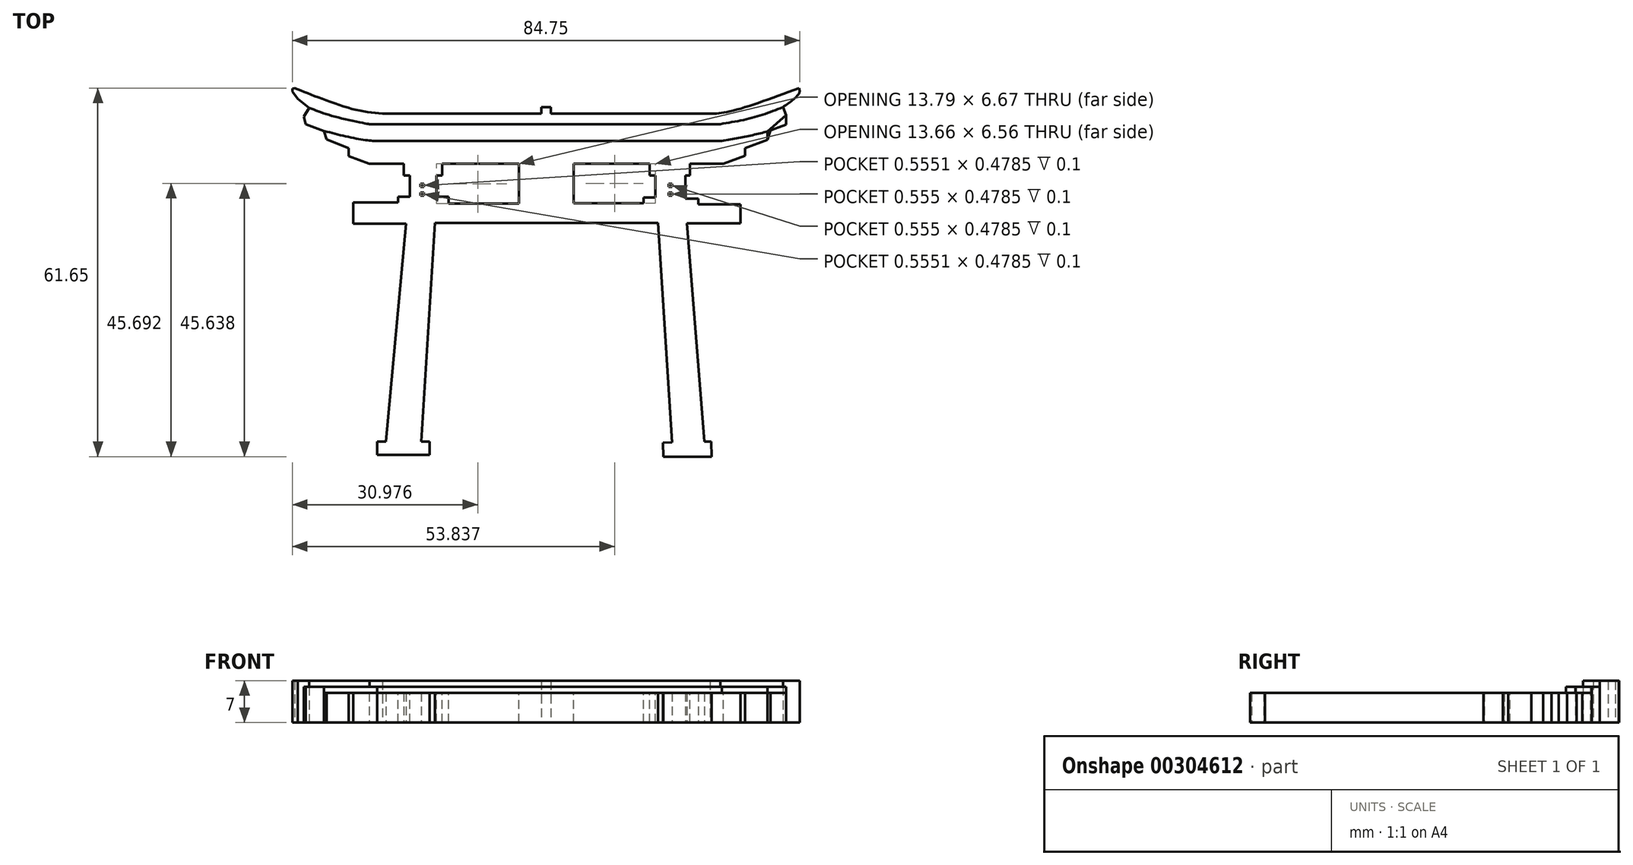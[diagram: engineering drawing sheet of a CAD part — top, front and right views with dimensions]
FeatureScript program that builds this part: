
annotation { "Feature Type Name" : "Feature", "Feature Type Description" : "" }
export const myFeature = defineFeature(function(context is Context, id is Id, definition is map)
    precondition{}
    {
        {
            var Q0;
            Q0=qCreatedBy(makeId("Top.planeOp"),FACE);
            var sketch = newSketch(context, id + "F0", { "sketchPlane" : qUnion([Q0])});
            skLineSegment(sketch, "E0", {"start": v(-21.15, -26.03) * mm, "end": v(-19.72, -26.03) * mm});
            skLineSegment(sketch, "E1", {"start": v(-19.72, -26.03) * mm, "end": v(-19.72, -28.26) * mm});
            skLineSegment(sketch, "E2", {"start": v(-19.72, -28.26) * mm, "end": v(-27.04, -28.26) * mm});
            skLineSegment(sketch, "E3", {"start": v(-23.64, 10.47) * mm, "end": v(-27.04, -26.03) * mm});
            skLineSegment(sketch, "E4", {"start": v(-27.04, -28.26) * mm, "end": v(-28.48, -28.26) * mm});
            skLineSegment(sketch, "E5", {"start": v(-28.48, -28.26) * mm, "end": v(-28.48, -26.03) * mm});
            skLineSegment(sketch, "E6", {"start": v(-28.48, -26.03) * mm, "end": v(-27.04, -26.03) * mm});
            skLineSegment(sketch, "E7", {"start": v(-23.64, 10.47) * mm, "end": v(-32.47, 10.47) * mm});
            skLineSegment(sketch, "E8", {"start": v(-32.47, 10.47) * mm, "end": v(-32.47, 13.97) * mm});
            skLineSegment(sketch, "E9", {"start": v(-23.34, 18.48) * mm, "end": v(-24.03, 18.48) * mm});
            skLineSegment(sketch, "E10", {"start": v(-24.03, 18.48) * mm, "end": v(-24.03, 20.45) * mm});
            skLineSegment(sketch, "E11", {"start": v(-24.03, 20.45) * mm, "end": v(-29.85, 20.45) * mm});
            skLineSegment(sketch, "E12", {"start": v(-29.85, 20.45) * mm, "end": v(-33.28, 21.76) * mm});
            skLineSegment(sketch, "E13", {"start": v(-33.28, 21.76) * mm, "end": v(-33.28, 23.07) * mm});
            skLineSegment(sketch, "E14", {"start": v(-33.28, 23.07) * mm, "end": v(-36.94, 24.53) * mm});
            skLineSegment(sketch, "E15", {"start": v(-36.94, 24.53) * mm, "end": v(-37.36, 25.95) * mm});
            skLineSegment(sketch, "E16", {"start": v(-37.36, 25.95) * mm, "end": v(-40.42, 27.1) * mm});
            skLineSegment(sketch, "E17", {"start": v(-40.42, 27.1) * mm, "end": v(-40.77, 28.34) * mm});
            skLineSegment(sketch, "E18", {"start": v(-40.77, 28.34) * mm, "end": v(-39.86, 29.83) * mm});
            skLineSegment(sketch, "E19", {"start": v(-39.86, 29.83) * mm, "end": v(-41.78, 31.32) * mm});
            skLineSegment(sketch, "E20", {"start": v(-41.78, 31.32) * mm, "end": v(-42.66, 32.53) * mm});
            skLineSegment(sketch, "E21", {"start": v(-42.66, 32.53) * mm, "end": v(-42.66, 33.02) * mm});
            skLineSegment(sketch, "E22", {"start": v(-42.66, 33.02) * mm, "end": v(-42.3, 33.13) * mm});
            skFitSpline(sketch, "E23", {"points": [v(-42.3, 33.13) * mm, v(-38.26, 31.54) * mm, v(-32.27, 29.54) * mm, v(-27.63, 28.83) * mm], "startDerivative": vector(12.27, -4.87) * mm, "endDerivative": vector(13.88, -1.37) * mm});
            skLineSegment(sketch, "E24", {"start": v(-27.63, 28.83) * mm, "end": v(-1.04, 28.83) * mm});
            skLineSegment(sketch, "E25", {"start": v(-1.04, 28.83) * mm, "end": v(-1.04, 29.95) * mm});
            skLineSegment(sketch, "E26", {"start": v(-1.04, 29.95) * mm, "end": v(0.56, 29.95) * mm});
            skLineSegment(sketch, "E27", {"start": v(0.56, 29.95) * mm, "end": v(0.56, 28.83) * mm});
            skLineSegment(sketch, "E28", {"start": v(0.56, 28.83) * mm, "end": v(27.15, 28.83) * mm});
            skFitSpline(sketch, "E29", {"points": [v(27.15, 28.83) * mm, v(30.3, 29.2) * mm, v(42.01, 33.12) * mm], "startDerivative": vector(7.99, 0.25) * mm, "endDerivative": vector(20.39, 7.52) * mm});
            skFitSpline(sketch, "E30", {"points": [v(42.01, 33.12) * mm, v(42.01, 32.3) * mm, v(39.3, 29.94) * mm], "startDerivative": vector(0.65, -2.38) * mm, "endDerivative": vector(-5.38, -3.62) * mm});
            skLineSegment(sketch, "E31", {"start": v(39.3, 29.94) * mm, "end": v(39.86, 28.6) * mm});
            skLineSegment(sketch, "E32", {"start": v(39.86, 28.6) * mm, "end": v(39.86, 27) * mm});
            skLineSegment(sketch, "E33", {"start": v(39.86, 27) * mm, "end": v(36.76, 25.88) * mm});
            skLineSegment(sketch, "E34", {"start": v(36.76, 25.88) * mm, "end": v(36.76, 24.44) * mm});
            skLineSegment(sketch, "E35", {"start": v(36.76, 24.44) * mm, "end": v(33, 23.07) * mm});
            skLineSegment(sketch, "E36", {"start": v(33, 23.07) * mm, "end": v(33, 21.83) * mm});
            skLineSegment(sketch, "E37", {"start": v(33, 21.83) * mm, "end": v(31.69, 20.91) * mm});
            skLineSegment(sketch, "E38", {"start": v(31.69, 20.91) * mm, "end": v(29.33, 20.2) * mm});
            skLineSegment(sketch, "E39", {"start": v(29.33, 20.2) * mm, "end": v(23.78, 20.2) * mm});
            skLineSegment(sketch, "E40", {"start": v(23.78, 20.2) * mm, "end": v(23.78, 18.16) * mm});
            skLineSegment(sketch, "E41", {"start": v(23.78, 18.16) * mm, "end": v(23, 18.16) * mm});
            skLineSegment(sketch, "E42", {"start": v(23, 18.16) * mm, "end": v(23, 14.64) * mm});
            skLineSegment(sketch, "E43", {"start": v(23, 14.64) * mm, "end": v(25.15, 14.64) * mm});
            skLineSegment(sketch, "E44", {"start": v(25.15, 14.64) * mm, "end": v(25.15, 13.7) * mm});
            skLineSegment(sketch, "E45", {"start": v(25.15, 13.7) * mm, "end": v(32.2, 13.7) * mm});
            skLineSegment(sketch, "E46", {"start": v(32.2, 13.7) * mm, "end": v(32.2, 10.51) * mm});
            skLineSegment(sketch, "E47", {"start": v(32.2, 10.51) * mm, "end": v(23.23, 10.51) * mm});
            skLineSegment(sketch, "E48", {"start": v(23.23, 10.51) * mm, "end": v(26.16, -26.03) * mm});
            skPoint(sketch, "E48.endSnap0", {"position": v(-20.43, -26.03) * mm});
            skLineSegment(sketch, "E49", {"start": v(27.39, -28.52) * mm, "end": v(19.31, -28.52) * mm});
            skLineSegment(sketch, "E50", {"start": v(19.31, -28.52) * mm, "end": v(19.25, -26.2) * mm});
            skLineSegment(sketch, "E51", {"start": v(19.25, -26.2) * mm, "end": v(20.8, -26.15) * mm});
            skLineSegment(sketch, "E52", {"start": v(20.8, -26.15) * mm, "end": v(18.45, 10.58) * mm});
            skLineSegment(sketch, "E53", {"start": v(18.45, 10.58) * mm, "end": v(-18.84, 10.58) * mm});
            skLineSegment(sketch, "E54", {"start": v(-18.84, 10.58) * mm, "end": v(-21.15, -26.03) * mm});
            skLineSegment(sketch, "E55", {"start": v(26.16, -26.03) * mm, "end": v(27.3, -26.03) * mm});
            skLineSegment(sketch, "E56", {"start": v(27.3, -26.03) * mm, "end": v(27.39, -28.52) * mm});
            skLineSegment(sketch, "E57", {"start": v(-23.34, 14.75) * mm, "end": v(-25.46, 14.75) * mm});
            skLineSegment(sketch, "E58", {"start": v(-25.46, 14.75) * mm, "end": v(-25.46, 13.97) * mm});
            skLineSegment(sketch, "E59", {"start": v(-25.46, 13.97) * mm, "end": v(-32.47, 13.97) * mm});
            skLineSegment(sketch, "E60", {"start": v(-23.34, 14.75) * mm, "end": v(-23.34, 18.48) * mm});
            skLineSegment(sketch, "E61", {"start": v(36.76, 24.44) * mm, "end": v(37.21, 26.05) * mm});
            skLineSegment(sketch, "E62", {"start": v(37.21, 26.05) * mm, "end": v(39.86, 27) * mm});
            skSolve(sketch);
        }
        {
            var Q0;
            Q0=makeQuery(id+"F0.imprint","IMPRINT",FACE,{"disambiguationData":[TD([[makeQuery(id+"F0.imprint","IMPRINT",EDGE,{"derivedFrom":sQuery(id+"F0.wireOp",EDGE,"E0")}),-1.0]])]});
            extrude(context, id + "F1", {"entities" : qUnion([Q0]), "depth" : 5 * mm});
        }
        {
            var Q0;
            Q0=makeQuery(id+"F1.opExtrude","CAP_FACE",FACE,{"disambiguationData":[OSD([sQuery(id+"F0.wireOp",EDGE,"E0"),sQuery(id+"F0.wireOp",EDGE,"E1"),sQuery(id+"F0.wireOp",EDGE,"E2"),sQuery(id+"F0.wireOp",EDGE,"E3"),sQuery(id+"F0.wireOp",EDGE,"E4"),sQuery(id+"F0.wireOp",EDGE,"E5"),sQuery(id+"F0.wireOp",EDGE,"E6"),sQuery(id+"F0.wireOp",EDGE,"E7"),sQuery(id+"F0.wireOp",EDGE,"E8"),sQuery(id+"F0.wireOp",EDGE,"E9"),sQuery(id+"F0.wireOp",EDGE,"E10"),sQuery(id+"F0.wireOp",EDGE,"E11"),sQuery(id+"F0.wireOp",EDGE,"E12"),sQuery(id+"F0.wireOp",EDGE,"E13"),sQuery(id+"F0.wireOp",EDGE,"E14"),sQuery(id+"F0.wireOp",EDGE,"E15"),sQuery(id+"F0.wireOp",EDGE,"E16"),sQuery(id+"F0.wireOp",EDGE,"E17"),sQuery(id+"F0.wireOp",EDGE,"E18"),sQuery(id+"F0.wireOp",EDGE,"E19"),sQuery(id+"F0.wireOp",EDGE,"E20"),sQuery(id+"F0.wireOp",EDGE,"E21"),sQuery(id+"F0.wireOp",EDGE,"E22"),sQuery(id+"F0.wireOp",EDGE,"E23"),sQuery(id+"F0.wireOp",EDGE,"E24"),sQuery(id+"F0.wireOp",EDGE,"E25"),sQuery(id+"F0.wireOp",EDGE,"E26"),sQuery(id+"F0.wireOp",EDGE,"E27"),sQuery(id+"F0.wireOp",EDGE,"E28"),sQuery(id+"F0.wireOp",EDGE,"E29"),sQuery(id+"F0.wireOp",EDGE,"E30"),sQuery(id+"F0.wireOp",EDGE,"E31"),sQuery(id+"F0.wireOp",EDGE,"E32"),sQuery(id+"F0.wireOp",EDGE,"E33"),sQuery(id+"F0.wireOp",EDGE,"E34"),sQuery(id+"F0.wireOp",EDGE,"E35"),sQuery(id+"F0.wireOp",EDGE,"E36"),sQuery(id+"F0.wireOp",EDGE,"E37"),sQuery(id+"F0.wireOp",EDGE,"E38"),sQuery(id+"F0.wireOp",EDGE,"E39"),sQuery(id+"F0.wireOp",EDGE,"E40"),sQuery(id+"F0.wireOp",EDGE,"E41"),sQuery(id+"F0.wireOp",EDGE,"E42"),sQuery(id+"F0.wireOp",EDGE,"E43"),sQuery(id+"F0.wireOp",EDGE,"E44"),sQuery(id+"F0.wireOp",EDGE,"E45"),sQuery(id+"F0.wireOp",EDGE,"E46"),sQuery(id+"F0.wireOp",EDGE,"E47"),sQuery(id+"F0.wireOp",EDGE,"E48"),sQuery(id+"F0.wireOp",EDGE,"E49"),sQuery(id+"F0.wireOp",EDGE,"E50"),sQuery(id+"F0.wireOp",EDGE,"E51"),sQuery(id+"F0.wireOp",EDGE,"E52"),sQuery(id+"F0.wireOp",EDGE,"E53"),sQuery(id+"F0.wireOp",EDGE,"E54"),sQuery(id+"F0.wireOp",EDGE,"E55"),sQuery(id+"F0.wireOp",EDGE,"E56"),sQuery(id+"F0.wireOp",EDGE,"E57"),sQuery(id+"F0.wireOp",EDGE,"E58"),sQuery(id+"F0.wireOp",EDGE,"E59"),sQuery(id+"F0.wireOp",EDGE,"E60")])],"isStart":false});
            var sketch = newSketch(context, id + "F2", { "sketchPlane" : qUnion([Q0])});
            skLineSegment(sketch, "E63", {"start": v(-17.65, 20.45) * mm, "end": v(-17.65, 18.48) * mm});
            skLineSegment(sketch, "E64", {"start": v(-17.65, 18.48) * mm, "end": v(-18.58, 18.48) * mm});
            skLineSegment(sketch, "E65", {"start": v(-18.58, 18.48) * mm, "end": v(-18.58, 14.95) * mm});
            skLineSegment(sketch, "E66", {"start": v(-18.58, 14.95) * mm, "end": v(-16.58, 14.95) * mm});
            skLineSegment(sketch, "E67", {"start": v(-16.58, 14.95) * mm, "end": v(-16.58, 13.78) * mm});
            skLineSegment(sketch, "E68", {"start": v(-16.58, 13.78) * mm, "end": v(-4.79, 13.78) * mm});
            skLineSegment(sketch, "E69", {"start": v(-4.79, 13.78) * mm, "end": v(-4.79, 20.45) * mm});
            skLineSegment(sketch, "E70", {"start": v(-4.79, 20.45) * mm, "end": v(-17.65, 20.45) * mm});
            skLineSegment(sketch, "E71", {"start": v(17.04, 20.45) * mm, "end": v(17.04, 18.48) * mm});
            skLineSegment(sketch, "E72", {"start": v(17.04, 18.48) * mm, "end": v(18, 18.48) * mm});
            skLineSegment(sketch, "E73", {"start": v(18, 18.48) * mm, "end": v(18, 14.81) * mm});
            skLineSegment(sketch, "E74", {"start": v(18, 14.81) * mm, "end": v(16.02, 14.81) * mm});
            skLineSegment(sketch, "E75", {"start": v(16.02, 14.81) * mm, "end": v(16.02, 13.9) * mm});
            skLineSegment(sketch, "E76", {"start": v(16.02, 13.9) * mm, "end": v(4.35, 13.9) * mm});
            skLineSegment(sketch, "E77", {"start": v(4.35, 13.9) * mm, "end": v(4.35, 20.45) * mm});
            skLineSegment(sketch, "E78", {"start": v(4.35, 20.45) * mm, "end": v(17.04, 20.45) * mm});
            skSolve(sketch);
        }
        {
            var Q0;
            Q0=makeQuery(id+"F2.imprint","IMPRINT",FACE,{"disambiguationData":[TD([[makeQuery(id+"F2.imprint","IMPRINT",EDGE,{"derivedFrom":sQuery(id+"F2.wireOp",EDGE,"E63")}),1.0]])]});
            var Q1;
            Q1=makeQuery(id+"F2.imprint","IMPRINT",FACE,{"disambiguationData":[TD([[makeQuery(id+"F2.imprint","IMPRINT",EDGE,{"derivedFrom":sQuery(id+"F2.wireOp",EDGE,"E71")}),-1.0]])]});
            extrude(context, id + "F3", {"entities" : qUnion([Q0, Q1]), "operationType" : NewBodyOperationType.REMOVE, "endBound" : BoundingType.THROUGH_ALL, "oppositeDirection" : true, "depth" : 25 * mm});
        }
        {
            var Q0;
            {var subQ0=sQuery(id+"F0.wireOp",EDGE,"E45");var subQ1=sQuery(id+"F0.wireOp",EDGE,"E44");var subQ2=sQuery(id+"F0.wireOp",EDGE,"E43");var subQ3=sQuery(id+"F0.wireOp",EDGE,"E42");var subQ4=sQuery(id+"F0.wireOp",EDGE,"E41");var subQ5=sQuery(id+"F0.wireOp",EDGE,"E40");var subQ6=sQuery(id+"F0.wireOp",EDGE,"E39");var subQ7=sQuery(id+"F0.wireOp",EDGE,"E38");var subQ8=sQuery(id+"F0.wireOp",EDGE,"E37");var subQ9=sQuery(id+"F0.wireOp",EDGE,"E36");var subQ10=sQuery(id+"F0.wireOp",EDGE,"E35");var subQ11=sQuery(id+"F0.wireOp",EDGE,"E34");var subQ12=sQuery(id+"F0.wireOp",EDGE,"E33");var subQ13=sQuery(id+"F0.wireOp",EDGE,"E32");var subQ14=sQuery(id+"F0.wireOp",EDGE,"E31");var subQ15=sQuery(id+"F0.wireOp",EDGE,"E30");var subQ16=sQuery(id+"F0.wireOp",EDGE,"E29");var subQ17=sQuery(id+"F0.wireOp",EDGE,"E28");var subQ18=sQuery(id+"F0.wireOp",EDGE,"E27");var subQ19=sQuery(id+"F0.wireOp",EDGE,"E26");var subQ20=sQuery(id+"F0.wireOp",EDGE,"E25");var subQ21=sQuery(id+"F0.wireOp",EDGE,"E24");var subQ22=sQuery(id+"F0.wireOp",EDGE,"E23");var subQ23=sQuery(id+"F0.wireOp",EDGE,"E9");var subQ24=sQuery(id+"F0.wireOp",EDGE,"E8");var subQ25=sQuery(id+"F0.wireOp",EDGE,"E7");var subQ26=sQuery(id+"F0.wireOp",EDGE,"E6");var subQ27=sQuery(id+"F0.wireOp",EDGE,"E5");var subQ28=sQuery(id+"F0.wireOp",EDGE,"E10");var subQ29=sQuery(id+"F0.wireOp",EDGE,"E46");var subQ30=sQuery(id+"F0.wireOp",EDGE,"E0");var subQ31=sQuery(id+"F0.wireOp",EDGE,"E22");var subQ32=sQuery(id+"F0.wireOp",EDGE,"E3");var subQ33=sQuery(id+"F0.wireOp",EDGE,"E1");var subQ34=sQuery(id+"F0.wireOp",EDGE,"E4");var subQ35=sQuery(id+"F0.wireOp",EDGE,"E2");var subQ36=sQuery(id+"F0.wireOp",EDGE,"E11");var subQ37=sQuery(id+"F0.wireOp",EDGE,"E12");var subQ38=sQuery(id+"F0.wireOp",EDGE,"E13");var subQ39=sQuery(id+"F0.wireOp",EDGE,"E14");var subQ40=sQuery(id+"F0.wireOp",EDGE,"E15");var subQ41=sQuery(id+"F0.wireOp",EDGE,"E16");var subQ42=sQuery(id+"F0.wireOp",EDGE,"E17");var subQ43=sQuery(id+"F0.wireOp",EDGE,"E18");var subQ44=sQuery(id+"F0.wireOp",EDGE,"E19");var subQ45=sQuery(id+"F0.wireOp",EDGE,"E20");var subQ46=sQuery(id+"F0.wireOp",EDGE,"E21");var subQ47=sQuery(id+"F0.wireOp",EDGE,"E47");var subQ48=sQuery(id+"F0.wireOp",EDGE,"E48");var subQ49=sQuery(id+"F0.wireOp",EDGE,"E49");var subQ50=sQuery(id+"F0.wireOp",EDGE,"E50");var subQ51=sQuery(id+"F0.wireOp",EDGE,"E51");var subQ52=sQuery(id+"F0.wireOp",EDGE,"E52");var subQ53=sQuery(id+"F0.wireOp",EDGE,"E53");var subQ54=sQuery(id+"F0.wireOp",EDGE,"E54");var subQ55=sQuery(id+"F0.wireOp",EDGE,"E55");var subQ56=sQuery(id+"F0.wireOp",EDGE,"E56");var subQ57=sQuery(id+"F0.wireOp",EDGE,"E57");var subQ58=sQuery(id+"F0.wireOp",EDGE,"E58");var subQ59=sQuery(id+"F0.wireOp",EDGE,"E59");var subQ60=sQuery(id+"F0.wireOp",EDGE,"E60");Q0=makeQuery(id+"FRBVWJomYvBm3HE_1.boolean.opBoolean","SPLIT",FACE,{"disambiguationData":[TD([makeQuery(id+"F1.opExtrude","SWEPT_FACE",FACE,{"disambiguationData":[OSD([subQ30])]})])],"derivedFrom":makeQuery(id+"F1.opExtrude","CAP_FACE",FACE,{"disambiguationData":[OSD([subQ30,subQ33,subQ35,subQ32,subQ34,subQ27,subQ26,subQ25,subQ24,subQ23,subQ28,subQ36,subQ37,subQ38,subQ39,subQ40,subQ41,subQ42,subQ43,subQ44,subQ45,subQ46,subQ31,subQ22,subQ21,subQ20,subQ19,subQ18,subQ17,subQ16,subQ15,subQ14,subQ13,subQ12,subQ11,subQ10,subQ9,subQ8,subQ7,subQ6,subQ5,subQ4,subQ3,subQ2,subQ1,subQ0,subQ29,subQ47,subQ48,subQ49,subQ50,subQ51,subQ52,subQ53,subQ54,subQ55,subQ56,subQ57,subQ58,subQ59,subQ60])],"isStart":false})});}
            var sketch = newSketch(context, id + "F4", { "sketchPlane" : qUnion([Q0])});
            skFitSpline(sketch, "E79", {"points": [v(-37.36, 25.95) * mm, v(-33.12, 24.92) * mm, v(-29.93, 24.37) * mm, v(-28.48, 24.27) * mm], "startDerivative": vector(10.45, -2.7) * mm, "endDerivative": vector(5.56, -0.21) * mm});
            skLineSegment(sketch, "E80", {"start": v(-28.48, 24.27) * mm, "end": v(29.09, 24.3) * mm});
            skFitSpline(sketch, "E81", {"points": [v(29.09, 24.3) * mm, v(33.26, 25.05) * mm, v(36.76, 25.88) * mm], "startDerivative": vector(8.2, 1.38) * mm, "endDerivative": vector(7.12, 1.81) * mm});
            skFitSpline(sketch, "E82", {"points": [v(-39.86, 29.83) * mm, v(-35.24, 28.27) * mm, v(-29.84, 27.1) * mm, v(-29.77, 27.1) * mm], "startDerivative": vector(8.57, -3.4) * mm, "endDerivative": vector(0.66, 0.12) * mm});
            skLineSegment(sketch, "E83", {"start": v(-29.77, 27.1) * mm, "end": v(28.82, 27.1) * mm});
            skFitSpline(sketch, "E84", {"points": [v(28.82, 27.1) * mm, v(34.5, 28.24) * mm, v(39.3, 29.94) * mm], "startDerivative": vector(11.26, 1.86) * mm, "endDerivative": vector(9.69, 3.82) * mm});
            skLineSegment(sketch, "E85", {"start": v(39.3, 29.94) * mm, "end": v(39.86, 28.6) * mm});
            skLineSegment(sketch, "E86", {"start": v(39.86, 28.6) * mm, "end": v(39.86, 28.6) * mm});
            skLineSegment(sketch, "E87", {"start": v(39.86, 28.6) * mm, "end": v(36.76, 25.88) * mm});
            skLineSegment(sketch, "E88", {"start": v(-39.86, 29.83) * mm, "end": v(-40.77, 28.34) * mm});
            skLineSegment(sketch, "E89", {"start": v(-40.77, 28.34) * mm, "end": v(-40.42, 27.1) * mm});
            skLineSegment(sketch, "E90", {"start": v(-40.42, 27.1) * mm, "end": v(-37.36, 25.95) * mm});
            skSolve(sketch);
        }
        {
            var Q0;
            Q0=makeQuery(id+"F4.imprint","IMPRINT",FACE,{"disambiguationData":[TD([[makeQuery(id+"F4.imprint","IMPRINT",EDGE,{"derivedFrom":sQuery(id+"F4.wireOp",EDGE,"E79")}),1.0]])]});
            extrude(context, id + "F5", {"entities" : qUnion([Q0]), "operationType" : NewBodyOperationType.ADD, "depth" : 1 * mm});
        }
        {
            var Q0;
            {var subQ0=sQuery(id+"F0.wireOp",EDGE,"E27");var subQ2=sQuery(id+"F0.wireOp",EDGE,"E26");var subQ4=sQuery(id+"F0.wireOp",EDGE,"E25");var subQ6=sQuery(id+"F0.wireOp",EDGE,"E24");var subQ8=sQuery(id+"F0.wireOp",EDGE,"E23");var subQ10=sQuery(id+"F0.wireOp",EDGE,"E22");var subQ12=sQuery(id+"F0.wireOp",EDGE,"E18");var subQ13=makeQuery(id+"F1.opExtrude","SWEPT_FACE",FACE,{"disambiguationData":[OSD([subQ12])]});var subQ14=sQuery(id+"F0.wireOp",EDGE,"E19");var subQ16=sQuery(id+"F0.wireOp",EDGE,"E20");var subQ18=sQuery(id+"F0.wireOp",EDGE,"E21");var subQ20=sQuery(id+"F0.wireOp",EDGE,"E28");var subQ22=sQuery(id+"F0.wireOp",EDGE,"E29");var subQ24=sQuery(id+"F0.wireOp",EDGE,"E30");var subQ26=sQuery(id+"F0.wireOp",EDGE,"E31");var subQ28=sQuery(id+"F0.wireOp",EDGE,"E45");var subQ29=sQuery(id+"F0.wireOp",EDGE,"E44");var subQ30=sQuery(id+"F0.wireOp",EDGE,"E43");var subQ31=sQuery(id+"F0.wireOp",EDGE,"E42");var subQ32=sQuery(id+"F0.wireOp",EDGE,"E41");var subQ33=sQuery(id+"F0.wireOp",EDGE,"E40");var subQ34=sQuery(id+"F0.wireOp",EDGE,"E39");var subQ35=sQuery(id+"F0.wireOp",EDGE,"E38");var subQ36=sQuery(id+"F0.wireOp",EDGE,"E37");var subQ37=sQuery(id+"F0.wireOp",EDGE,"E36");var subQ38=sQuery(id+"F0.wireOp",EDGE,"E35");var subQ39=sQuery(id+"F0.wireOp",EDGE,"E34");var subQ40=sQuery(id+"F0.wireOp",EDGE,"E33");var subQ41=sQuery(id+"F0.wireOp",EDGE,"E32");var subQ42=sQuery(id+"F0.wireOp",EDGE,"E9");var subQ43=sQuery(id+"F0.wireOp",EDGE,"E8");var subQ44=sQuery(id+"F0.wireOp",EDGE,"E7");var subQ45=sQuery(id+"F0.wireOp",EDGE,"E6");var subQ46=sQuery(id+"F0.wireOp",EDGE,"E5");var subQ47=sQuery(id+"F0.wireOp",EDGE,"E10");var subQ48=sQuery(id+"F0.wireOp",EDGE,"E46");var subQ49=sQuery(id+"F0.wireOp",EDGE,"E0");var subQ50=sQuery(id+"F0.wireOp",EDGE,"E3");var subQ51=sQuery(id+"F0.wireOp",EDGE,"E1");var subQ52=sQuery(id+"F0.wireOp",EDGE,"E4");var subQ53=sQuery(id+"F0.wireOp",EDGE,"E2");var subQ54=sQuery(id+"F0.wireOp",EDGE,"E11");var subQ55=sQuery(id+"F0.wireOp",EDGE,"E12");var subQ56=sQuery(id+"F0.wireOp",EDGE,"E13");var subQ57=sQuery(id+"F0.wireOp",EDGE,"E14");var subQ58=sQuery(id+"F0.wireOp",EDGE,"E15");var subQ59=sQuery(id+"F0.wireOp",EDGE,"E16");var subQ60=sQuery(id+"F0.wireOp",EDGE,"E17");var subQ61=sQuery(id+"F0.wireOp",EDGE,"E47");var subQ62=sQuery(id+"F0.wireOp",EDGE,"E48");var subQ63=sQuery(id+"F0.wireOp",EDGE,"E49");var subQ64=sQuery(id+"F0.wireOp",EDGE,"E50");var subQ65=sQuery(id+"F0.wireOp",EDGE,"E51");var subQ66=sQuery(id+"F0.wireOp",EDGE,"E52");var subQ67=sQuery(id+"F0.wireOp",EDGE,"E53");var subQ68=sQuery(id+"F0.wireOp",EDGE,"E54");var subQ69=sQuery(id+"F0.wireOp",EDGE,"E55");var subQ70=sQuery(id+"F0.wireOp",EDGE,"E56");var subQ71=sQuery(id+"F0.wireOp",EDGE,"E57");var subQ72=sQuery(id+"F0.wireOp",EDGE,"E58");var subQ73=sQuery(id+"F0.wireOp",EDGE,"E59");var subQ74=sQuery(id+"F0.wireOp",EDGE,"E60");Q0=makeQuery(id+"F5.boolean.opBoolean","SPLIT",FACE,{"disambiguationData":[TD([subQ13])],"derivedFrom":makeQuery(id+"FRBVWJomYvBm3HE_1.boolean.opBoolean","SPLIT",FACE,{"disambiguationData":[TD([makeQuery(id+"F1.opExtrude","SWEPT_FACE",FACE,{"disambiguationData":[OSD([subQ49])]})])],"derivedFrom":makeQuery(id+"F1.opExtrude","CAP_FACE",FACE,{"disambiguationData":[OSD([subQ49,subQ51,subQ53,subQ50,subQ52,subQ46,subQ45,subQ44,subQ43,subQ42,subQ47,subQ54,subQ55,subQ56,subQ57,subQ58,subQ59,subQ60,subQ12,subQ14,subQ16,subQ18,subQ10,subQ8,subQ6,subQ4,subQ2,subQ0,subQ20,subQ22,subQ24,subQ26,subQ41,subQ40,subQ39,subQ38,subQ37,subQ36,subQ35,subQ34,subQ33,subQ32,subQ31,subQ30,subQ29,subQ28,subQ48,subQ61,subQ62,subQ63,subQ64,subQ65,subQ66,subQ67,subQ68,subQ69,subQ70,subQ71,subQ72,subQ73,subQ74])],"isStart":false})})});}
            extrude(context, id + "F6", {"entities" : qUnion([Q0]), "operationType" : NewBodyOperationType.ADD, "depth" : 2 * mm});
        }
        {
            var Q0;
            {var subQ0=sQuery(id+"F0.wireOp",EDGE,"E48");var subQ2=sQuery(id+"F0.wireOp",EDGE,"E47");var subQ5=sQuery(id+"F0.wireOp",EDGE,"E45");var subQ7=sQuery(id+"F0.wireOp",EDGE,"E44");var subQ9=sQuery(id+"F0.wireOp",EDGE,"E43");var subQ11=sQuery(id+"F0.wireOp",EDGE,"E42");var subQ13=sQuery(id+"F0.wireOp",EDGE,"E41");var subQ15=sQuery(id+"F0.wireOp",EDGE,"E40");var subQ17=sQuery(id+"F0.wireOp",EDGE,"E39");var subQ19=sQuery(id+"F0.wireOp",EDGE,"E56");var subQ21=sQuery(id+"F0.wireOp",EDGE,"E9");var subQ23=sQuery(id+"F0.wireOp",EDGE,"E55");var subQ25=sQuery(id+"F0.wireOp",EDGE,"E8");var subQ27=sQuery(id+"F0.wireOp",EDGE,"E54");var subQ29=sQuery(id+"F0.wireOp",EDGE,"E7");var subQ32=sQuery(id+"F0.wireOp",EDGE,"E53");var subQ34=sQuery(id+"F0.wireOp",EDGE,"E6");var subQ37=sQuery(id+"F0.wireOp",EDGE,"E52");var subQ39=sQuery(id+"F0.wireOp",EDGE,"E5");var subQ41=sQuery(id+"F0.wireOp",EDGE,"E57");var subQ43=sQuery(id+"F0.wireOp",EDGE,"E10");var subQ45=sQuery(id+"F0.wireOp",EDGE,"E33");var subQ48=sQuery(id+"F0.wireOp",EDGE,"E46");var subQ50=sQuery(id+"F0.wireOp",EDGE,"E0");var subQ51=makeQuery(id+"F1.opExtrude","SWEPT_FACE",FACE,{"disambiguationData":[OSD([subQ50])]});var subQ52=sQuery(id+"F0.wireOp",EDGE,"E51");var subQ55=sQuery(id+"F0.wireOp",EDGE,"E3");var subQ57=sQuery(id+"F0.wireOp",EDGE,"E49");var subQ60=sQuery(id+"F0.wireOp",EDGE,"E1");var subQ62=sQuery(id+"F0.wireOp",EDGE,"E50");var subQ65=sQuery(id+"F0.wireOp",EDGE,"E4");var subQ66=sQuery(id+"F0.wireOp",EDGE,"E2");var subQ68=sQuery(id+"F0.wireOp",EDGE,"E58");var subQ70=sQuery(id+"F0.wireOp",EDGE,"E11");var subQ72=sQuery(id+"F0.wireOp",EDGE,"E34");var subQ75=sQuery(id+"F0.wireOp",EDGE,"E59");var subQ77=sQuery(id+"F0.wireOp",EDGE,"E12");var subQ79=sQuery(id+"F0.wireOp",EDGE,"E35");var subQ82=sQuery(id+"F0.wireOp",EDGE,"E60");var subQ84=sQuery(id+"F0.wireOp",EDGE,"E13");var subQ86=sQuery(id+"F0.wireOp",EDGE,"E36");var subQ89=sQuery(id+"F0.wireOp",EDGE,"E14");var subQ91=sQuery(id+"F0.wireOp",EDGE,"E37");var subQ94=sQuery(id+"F0.wireOp",EDGE,"E15");var subQ96=sQuery(id+"F0.wireOp",EDGE,"E38");var subQ99=sQuery(id+"F0.wireOp",EDGE,"E16");var subQ109=sQuery(id+"F0.wireOp",EDGE,"E32");var subQ110=sQuery(id+"F0.wireOp",EDGE,"E31");var subQ111=sQuery(id+"F0.wireOp",EDGE,"E30");var subQ112=sQuery(id+"F0.wireOp",EDGE,"E29");var subQ113=sQuery(id+"F0.wireOp",EDGE,"E28");var subQ114=sQuery(id+"F0.wireOp",EDGE,"E27");var subQ115=sQuery(id+"F0.wireOp",EDGE,"E26");var subQ116=sQuery(id+"F0.wireOp",EDGE,"E25");var subQ117=sQuery(id+"F0.wireOp",EDGE,"E24");var subQ118=sQuery(id+"F0.wireOp",EDGE,"E23");var subQ119=sQuery(id+"F0.wireOp",EDGE,"E22");var subQ120=sQuery(id+"F0.wireOp",EDGE,"E17");var subQ121=sQuery(id+"F0.wireOp",EDGE,"E18");var subQ122=sQuery(id+"F0.wireOp",EDGE,"E19");var subQ123=sQuery(id+"F0.wireOp",EDGE,"E20");var subQ124=sQuery(id+"F0.wireOp",EDGE,"E21");Q0=makeQuery(id+"F5.boolean.opBoolean","SPLIT",FACE,{"disambiguationData":[TD([subQ51])],"derivedFrom":makeQuery(id+"FRBVWJomYvBm3HE_1.boolean.opBoolean","SPLIT",FACE,{"disambiguationData":[TD([subQ51])],"derivedFrom":makeQuery(id+"F1.opExtrude","CAP_FACE",FACE,{"disambiguationData":[OSD([subQ50,subQ60,subQ66,subQ55,subQ65,subQ39,subQ34,subQ29,subQ25,subQ21,subQ43,subQ70,subQ77,subQ84,subQ89,subQ94,subQ99,subQ120,subQ121,subQ122,subQ123,subQ124,subQ119,subQ118,subQ117,subQ116,subQ115,subQ114,subQ113,subQ112,subQ111,subQ110,subQ109,subQ45,subQ72,subQ79,subQ86,subQ91,subQ96,subQ17,subQ15,subQ13,subQ11,subQ9,subQ7,subQ5,subQ48,subQ2,subQ0,subQ57,subQ62,subQ52,subQ37,subQ32,subQ27,subQ23,subQ19,subQ41,subQ68,subQ75,subQ82])],"isStart":false})})});}
            var sketch = newSketch(context, id + "F7", { "sketchPlane" : qUnion([Q0])});
            skLineSegment(sketch, "E91", {"start": v(23, 18.48) * mm, "end": v(23, 14.64) * mm});
            skLineSegment(sketch, "E92", {"start": v(23, 18.48) * mm, "end": v(23.78, 18.48) * mm});
            skLineSegment(sketch, "E93", {"start": v(23.78, 18.48) * mm, "end": v(23.78, 20.45) * mm});
            skLineSegment(sketch, "E94", {"start": v(23.78, 20.45) * mm, "end": v(29.33, 20.45) * mm});
            skLineSegment(sketch, "E95", {"start": v(29.33, 20.45) * mm, "end": v(33, 21.83) * mm});
            skSolve(sketch);
        }
        {
            var Q0;
            {var subQ0=sQuery(id+"F7.wireOp",EDGE,"E94");Q0=makeQuery(id+"F7.imprint","IMPRINT",FACE,{"disambiguationData":[TD([[makeQuery(id+"F7.imprint","IMPRINT",EDGE,{"derivedFrom":subQ0}),-1.0]])]});}
            extrude(context, id + "F8", {"entities" : qUnion([Q0]), "operationType" : NewBodyOperationType.REMOVE, "oppositeDirection" : true, "depth" : 25 * mm});
        }
        {
            var Q0;
            Q0=makeQuery(id+"F0.imprint","IMPRINT",FACE,{"disambiguationData":[TD([[makeQuery(id+"F0.imprint","IMPRINT",EDGE,{"derivedFrom":sQuery(id+"F0.wireOp",EDGE,"E33")}),1.0]])]});
            extrude(context, id + "F9", {"entities" : qUnion([Q0]), "depth" : 5 * mm});
        }
        {
            var Q0;
            {var subQ0=sQuery(id+"F0.wireOp",EDGE,"E47");var subQ3=sQuery(id+"F0.wireOp",EDGE,"E45");var subQ5=sQuery(id+"F0.wireOp",EDGE,"E44");var subQ7=sQuery(id+"F0.wireOp",EDGE,"E43");var subQ9=sQuery(id+"F0.wireOp",EDGE,"E42");var subQ11=sQuery(id+"F0.wireOp",EDGE,"E41");var subQ13=sQuery(id+"F0.wireOp",EDGE,"E40");var subQ15=sQuery(id+"F0.wireOp",EDGE,"E39");var subQ17=sQuery(id+"F0.wireOp",EDGE,"E38");var subQ20=sQuery(id+"F0.wireOp",EDGE,"E56");var subQ22=sQuery(id+"F0.wireOp",EDGE,"E9");var subQ24=sQuery(id+"F0.wireOp",EDGE,"E55");var subQ26=sQuery(id+"F0.wireOp",EDGE,"E8");var subQ28=sQuery(id+"F0.wireOp",EDGE,"E54");var subQ30=sQuery(id+"F0.wireOp",EDGE,"E7");var subQ32=sQuery(id+"F0.wireOp",EDGE,"E53");var subQ34=sQuery(id+"F0.wireOp",EDGE,"E6");var subQ37=sQuery(id+"F0.wireOp",EDGE,"E52");var subQ39=sQuery(id+"F0.wireOp",EDGE,"E5");var subQ41=sQuery(id+"F0.wireOp",EDGE,"E51");var subQ44=sQuery(id+"F0.wireOp",EDGE,"E3");var subQ46=sQuery(id+"F0.wireOp",EDGE,"E46");var subQ48=sQuery(id+"F0.wireOp",EDGE,"E0");var subQ49=makeQuery(id+"F1.opExtrude","SWEPT_FACE",FACE,{"disambiguationData":[OSD([subQ48])]});var subQ50=sQuery(id+"F0.wireOp",EDGE,"E48");var subQ52=sQuery(id+"F0.wireOp",EDGE,"E62");var subQ53=sQuery(id+"F0.wireOp",EDGE,"E60");var subQ54=sQuery(id+"F0.wireOp",EDGE,"E59");var subQ55=sQuery(id+"F0.wireOp",EDGE,"E58");var subQ56=sQuery(id+"F0.wireOp",EDGE,"E57");var subQ57=sQuery(id+"F0.wireOp",EDGE,"E50");var subQ58=sQuery(id+"F0.wireOp",EDGE,"E49");var subQ59=sQuery(id+"F0.wireOp",EDGE,"E37");var subQ60=sQuery(id+"F0.wireOp",EDGE,"E36");var subQ61=sQuery(id+"F0.wireOp",EDGE,"E35");var subQ62=sQuery(id+"F0.wireOp",EDGE,"E34");var subQ63=sQuery(id+"F0.wireOp",EDGE,"E33");var subQ64=sQuery(id+"F0.wireOp",EDGE,"E32");var subQ65=sQuery(id+"F0.wireOp",EDGE,"E31");var subQ66=sQuery(id+"F0.wireOp",EDGE,"E30");var subQ67=sQuery(id+"F0.wireOp",EDGE,"E29");var subQ68=sQuery(id+"F0.wireOp",EDGE,"E28");var subQ69=sQuery(id+"F0.wireOp",EDGE,"E27");var subQ70=sQuery(id+"F0.wireOp",EDGE,"E26");var subQ71=sQuery(id+"F0.wireOp",EDGE,"E25");var subQ72=sQuery(id+"F0.wireOp",EDGE,"E24");var subQ73=sQuery(id+"F0.wireOp",EDGE,"E23");var subQ74=sQuery(id+"F0.wireOp",EDGE,"E22");var subQ75=sQuery(id+"F0.wireOp",EDGE,"E21");var subQ76=sQuery(id+"F0.wireOp",EDGE,"E20");var subQ77=sQuery(id+"F0.wireOp",EDGE,"E19");var subQ78=sQuery(id+"F0.wireOp",EDGE,"E18");var subQ79=sQuery(id+"F0.wireOp",EDGE,"E17");var subQ80=sQuery(id+"F0.wireOp",EDGE,"E16");var subQ81=sQuery(id+"F0.wireOp",EDGE,"E15");var subQ82=sQuery(id+"F0.wireOp",EDGE,"E14");var subQ83=sQuery(id+"F0.wireOp",EDGE,"E13");var subQ84=sQuery(id+"F0.wireOp",EDGE,"E12");var subQ85=sQuery(id+"F0.wireOp",EDGE,"E11");var subQ86=sQuery(id+"F0.wireOp",EDGE,"E10");var subQ87=sQuery(id+"F0.wireOp",EDGE,"E4");var subQ88=sQuery(id+"F0.wireOp",EDGE,"E2");var subQ89=sQuery(id+"F0.wireOp",EDGE,"E1");var subQ90=makeQuery(id+"F1.opExtrude","CAP_FACE",FACE,{"disambiguationData":[OSD([subQ48,subQ89,subQ88,subQ44,subQ87,subQ39,subQ34,subQ30,subQ26,subQ22,subQ86,subQ85,subQ84,subQ83,subQ82,subQ81,subQ80,subQ79,subQ78,subQ77,subQ76,subQ75,subQ74,subQ73,subQ72,subQ71,subQ70,subQ69,subQ68,subQ67,subQ66,subQ65,subQ64,subQ63,subQ62,subQ61,subQ60,subQ59,subQ17,subQ15,subQ13,subQ11,subQ9,subQ7,subQ5,subQ3,subQ46,subQ0,subQ50,subQ58,subQ57,subQ41,subQ37,subQ32,subQ28,subQ24,subQ20,subQ56,subQ55,subQ54,subQ53,subQ52])],"isStart":false});Q0=makeQuery(id+"F5.boolean.opBoolean","SPLIT",FACE,{"disambiguationData":[TD([subQ49])],"derivedFrom":makeQuery(id+"FRBVWJomYvBm3HE_1.boolean.opBoolean","SPLIT",FACE,{"disambiguationData":[TD([subQ49])],"derivedFrom":subQ90})});}
            var sketch = newSketch(context, id + "F10", { "sketchPlane" : qUnion([Q0])});
            skLineSegment(sketch, "E96", {"start": v(23, 14.64) * mm, "end": v(23, 18.48) * mm});
            skLineSegment(sketch, "E97", {"start": v(23, 18.48) * mm, "end": v(23.78, 18.48) * mm});
            skSolve(sketch);
        }
        {
            var Q0;
            {var subQ2=sQuery(id+"F10.wireOp",EDGE,"E97");Q0=makeQuery(id+"F10.imprint","IMPRINT",FACE,{"disambiguationData":[TD([[makeQuery(id+"F10.imprint","IMPRINT",EDGE,{"derivedFrom":subQ2}),-1.0]])]});}
            extrude(context, id + "F11", {"entities" : qUnion([Q0]), "operationType" : NewBodyOperationType.REMOVE, "oppositeDirection" : true, "depth" : 25 * mm});
        }
        {
            var Q0;
            {var subQ0=sQuery(id+"F0.wireOp",EDGE,"E47");var subQ3=sQuery(id+"F0.wireOp",EDGE,"E45");var subQ5=sQuery(id+"F0.wireOp",EDGE,"E44");var subQ7=sQuery(id+"F0.wireOp",EDGE,"E43");var subQ9=sQuery(id+"F0.wireOp",EDGE,"E42");var subQ11=sQuery(id+"F0.wireOp",EDGE,"E41");var subQ13=sQuery(id+"F0.wireOp",EDGE,"E40");var subQ15=sQuery(id+"F0.wireOp",EDGE,"E39");var subQ17=sQuery(id+"F0.wireOp",EDGE,"E38");var subQ20=sQuery(id+"F0.wireOp",EDGE,"E56");var subQ22=sQuery(id+"F0.wireOp",EDGE,"E9");var subQ24=sQuery(id+"F0.wireOp",EDGE,"E55");var subQ26=sQuery(id+"F0.wireOp",EDGE,"E8");var subQ28=sQuery(id+"F0.wireOp",EDGE,"E54");var subQ30=sQuery(id+"F0.wireOp",EDGE,"E7");var subQ32=sQuery(id+"F0.wireOp",EDGE,"E53");var subQ34=sQuery(id+"F0.wireOp",EDGE,"E6");var subQ37=sQuery(id+"F0.wireOp",EDGE,"E52");var subQ39=sQuery(id+"F0.wireOp",EDGE,"E5");var subQ41=sQuery(id+"F0.wireOp",EDGE,"E51");var subQ44=sQuery(id+"F0.wireOp",EDGE,"E3");var subQ46=sQuery(id+"F0.wireOp",EDGE,"E46");var subQ48=sQuery(id+"F0.wireOp",EDGE,"E0");var subQ49=makeQuery(id+"F1.opExtrude","SWEPT_FACE",FACE,{"disambiguationData":[OSD([subQ48])]});var subQ50=sQuery(id+"F0.wireOp",EDGE,"E48");var subQ52=sQuery(id+"F0.wireOp",EDGE,"E62");var subQ53=sQuery(id+"F0.wireOp",EDGE,"E60");var subQ54=sQuery(id+"F0.wireOp",EDGE,"E59");var subQ55=sQuery(id+"F0.wireOp",EDGE,"E58");var subQ56=sQuery(id+"F0.wireOp",EDGE,"E57");var subQ57=sQuery(id+"F0.wireOp",EDGE,"E50");var subQ58=sQuery(id+"F0.wireOp",EDGE,"E49");var subQ59=sQuery(id+"F0.wireOp",EDGE,"E37");var subQ60=sQuery(id+"F0.wireOp",EDGE,"E36");var subQ61=sQuery(id+"F0.wireOp",EDGE,"E35");var subQ62=sQuery(id+"F0.wireOp",EDGE,"E34");var subQ63=sQuery(id+"F0.wireOp",EDGE,"E33");var subQ64=sQuery(id+"F0.wireOp",EDGE,"E32");var subQ65=sQuery(id+"F0.wireOp",EDGE,"E31");var subQ66=sQuery(id+"F0.wireOp",EDGE,"E30");var subQ67=sQuery(id+"F0.wireOp",EDGE,"E29");var subQ68=sQuery(id+"F0.wireOp",EDGE,"E28");var subQ69=sQuery(id+"F0.wireOp",EDGE,"E27");var subQ70=sQuery(id+"F0.wireOp",EDGE,"E26");var subQ71=sQuery(id+"F0.wireOp",EDGE,"E25");var subQ72=sQuery(id+"F0.wireOp",EDGE,"E24");var subQ73=sQuery(id+"F0.wireOp",EDGE,"E23");var subQ74=sQuery(id+"F0.wireOp",EDGE,"E22");var subQ75=sQuery(id+"F0.wireOp",EDGE,"E21");var subQ76=sQuery(id+"F0.wireOp",EDGE,"E20");var subQ77=sQuery(id+"F0.wireOp",EDGE,"E19");var subQ78=sQuery(id+"F0.wireOp",EDGE,"E18");var subQ79=sQuery(id+"F0.wireOp",EDGE,"E17");var subQ80=sQuery(id+"F0.wireOp",EDGE,"E16");var subQ81=sQuery(id+"F0.wireOp",EDGE,"E15");var subQ82=sQuery(id+"F0.wireOp",EDGE,"E14");var subQ83=sQuery(id+"F0.wireOp",EDGE,"E13");var subQ84=sQuery(id+"F0.wireOp",EDGE,"E12");var subQ85=sQuery(id+"F0.wireOp",EDGE,"E11");var subQ86=sQuery(id+"F0.wireOp",EDGE,"E10");var subQ87=sQuery(id+"F0.wireOp",EDGE,"E4");var subQ88=sQuery(id+"F0.wireOp",EDGE,"E2");var subQ89=sQuery(id+"F0.wireOp",EDGE,"E1");var subQ90=makeQuery(id+"F1.opExtrude","CAP_FACE",FACE,{"disambiguationData":[OSD([subQ48,subQ89,subQ88,subQ44,subQ87,subQ39,subQ34,subQ30,subQ26,subQ22,subQ86,subQ85,subQ84,subQ83,subQ82,subQ81,subQ80,subQ79,subQ78,subQ77,subQ76,subQ75,subQ74,subQ73,subQ72,subQ71,subQ70,subQ69,subQ68,subQ67,subQ66,subQ65,subQ64,subQ63,subQ62,subQ61,subQ60,subQ59,subQ17,subQ15,subQ13,subQ11,subQ9,subQ7,subQ5,subQ3,subQ46,subQ0,subQ50,subQ58,subQ57,subQ41,subQ37,subQ32,subQ28,subQ24,subQ20,subQ56,subQ55,subQ54,subQ53,subQ52])],"isStart":false});Q0=makeQuery(id+"F5.boolean.opBoolean","SPLIT",FACE,{"disambiguationData":[TD([subQ49])],"derivedFrom":makeQuery(id+"FRBVWJomYvBm3HE_1.boolean.opBoolean","SPLIT",FACE,{"disambiguationData":[TD([subQ49])],"derivedFrom":subQ90})});}
            var sketch = newSketch(context, id + "F12", { "sketchPlane" : qUnion([Q0])});
            skLineSegment(sketch, "E98", {"start": v(-23.34, 14.75) * mm, "end": v(-23.01, 14.75) * mm});
            skLineSegment(sketch, "E99", {"start": v(-23.01, 14.75) * mm, "end": v(-23.01, 18.48) * mm});
            skLineSegment(sketch, "E100", {"start": v(-23.01, 18.48) * mm, "end": v(-24.03, 18.48) * mm});
            skSolve(sketch);
        }
        {
            var Q0;
            Q0=makeQuery(id+"F12.imprint","IMPRINT",FACE,{"disambiguationData":[TD([[makeQuery(id+"F12.imprint","IMPRINT",EDGE,{"derivedFrom":sQuery(id+"F12.wireOp",EDGE,"E98")}),1.0]])]});
            extrude(context, id + "F13", {"entities" : qUnion([Q0]), "operationType" : NewBodyOperationType.REMOVE, "oppositeDirection" : true, "depth" : 25 * mm});
        }
        {
            var Q0;
            {var subQ0=sQuery(id+"F0.wireOp",EDGE,"E47");var subQ3=sQuery(id+"F0.wireOp",EDGE,"E45");var subQ5=sQuery(id+"F0.wireOp",EDGE,"E44");var subQ7=sQuery(id+"F0.wireOp",EDGE,"E43");var subQ9=sQuery(id+"F0.wireOp",EDGE,"E42");var subQ11=sQuery(id+"F0.wireOp",EDGE,"E41");var subQ13=sQuery(id+"F0.wireOp",EDGE,"E40");var subQ15=sQuery(id+"F0.wireOp",EDGE,"E39");var subQ17=sQuery(id+"F0.wireOp",EDGE,"E38");var subQ20=sQuery(id+"F0.wireOp",EDGE,"E56");var subQ22=sQuery(id+"F0.wireOp",EDGE,"E9");var subQ24=sQuery(id+"F0.wireOp",EDGE,"E55");var subQ26=sQuery(id+"F0.wireOp",EDGE,"E8");var subQ28=sQuery(id+"F0.wireOp",EDGE,"E54");var subQ30=sQuery(id+"F0.wireOp",EDGE,"E7");var subQ32=sQuery(id+"F0.wireOp",EDGE,"E53");var subQ34=sQuery(id+"F0.wireOp",EDGE,"E6");var subQ37=sQuery(id+"F0.wireOp",EDGE,"E52");var subQ39=sQuery(id+"F0.wireOp",EDGE,"E5");var subQ41=sQuery(id+"F0.wireOp",EDGE,"E51");var subQ44=sQuery(id+"F0.wireOp",EDGE,"E3");var subQ46=sQuery(id+"F0.wireOp",EDGE,"E46");var subQ48=sQuery(id+"F0.wireOp",EDGE,"E0");var subQ49=makeQuery(id+"F1.opExtrude","SWEPT_FACE",FACE,{"disambiguationData":[OSD([subQ48])]});var subQ50=sQuery(id+"F0.wireOp",EDGE,"E48");var subQ52=sQuery(id+"F0.wireOp",EDGE,"E62");var subQ53=sQuery(id+"F0.wireOp",EDGE,"E60");var subQ54=sQuery(id+"F0.wireOp",EDGE,"E59");var subQ55=sQuery(id+"F0.wireOp",EDGE,"E58");var subQ56=sQuery(id+"F0.wireOp",EDGE,"E57");var subQ57=sQuery(id+"F0.wireOp",EDGE,"E50");var subQ58=sQuery(id+"F0.wireOp",EDGE,"E49");var subQ59=sQuery(id+"F0.wireOp",EDGE,"E37");var subQ60=sQuery(id+"F0.wireOp",EDGE,"E36");var subQ61=sQuery(id+"F0.wireOp",EDGE,"E35");var subQ62=sQuery(id+"F0.wireOp",EDGE,"E34");var subQ63=sQuery(id+"F0.wireOp",EDGE,"E33");var subQ64=sQuery(id+"F0.wireOp",EDGE,"E32");var subQ65=sQuery(id+"F0.wireOp",EDGE,"E31");var subQ66=sQuery(id+"F0.wireOp",EDGE,"E30");var subQ67=sQuery(id+"F0.wireOp",EDGE,"E29");var subQ68=sQuery(id+"F0.wireOp",EDGE,"E28");var subQ69=sQuery(id+"F0.wireOp",EDGE,"E27");var subQ70=sQuery(id+"F0.wireOp",EDGE,"E26");var subQ71=sQuery(id+"F0.wireOp",EDGE,"E25");var subQ72=sQuery(id+"F0.wireOp",EDGE,"E24");var subQ73=sQuery(id+"F0.wireOp",EDGE,"E23");var subQ74=sQuery(id+"F0.wireOp",EDGE,"E22");var subQ75=sQuery(id+"F0.wireOp",EDGE,"E21");var subQ76=sQuery(id+"F0.wireOp",EDGE,"E20");var subQ77=sQuery(id+"F0.wireOp",EDGE,"E19");var subQ78=sQuery(id+"F0.wireOp",EDGE,"E18");var subQ79=sQuery(id+"F0.wireOp",EDGE,"E17");var subQ80=sQuery(id+"F0.wireOp",EDGE,"E16");var subQ81=sQuery(id+"F0.wireOp",EDGE,"E15");var subQ82=sQuery(id+"F0.wireOp",EDGE,"E14");var subQ83=sQuery(id+"F0.wireOp",EDGE,"E13");var subQ84=sQuery(id+"F0.wireOp",EDGE,"E12");var subQ85=sQuery(id+"F0.wireOp",EDGE,"E11");var subQ86=sQuery(id+"F0.wireOp",EDGE,"E10");var subQ87=sQuery(id+"F0.wireOp",EDGE,"E4");var subQ88=sQuery(id+"F0.wireOp",EDGE,"E2");var subQ89=sQuery(id+"F0.wireOp",EDGE,"E1");var subQ90=makeQuery(id+"F1.opExtrude","CAP_FACE",FACE,{"disambiguationData":[OSD([subQ48,subQ89,subQ88,subQ44,subQ87,subQ39,subQ34,subQ30,subQ26,subQ22,subQ86,subQ85,subQ84,subQ83,subQ82,subQ81,subQ80,subQ79,subQ78,subQ77,subQ76,subQ75,subQ74,subQ73,subQ72,subQ71,subQ70,subQ69,subQ68,subQ67,subQ66,subQ65,subQ64,subQ63,subQ62,subQ61,subQ60,subQ59,subQ17,subQ15,subQ13,subQ11,subQ9,subQ7,subQ5,subQ3,subQ46,subQ0,subQ50,subQ58,subQ57,subQ41,subQ37,subQ32,subQ28,subQ24,subQ20,subQ56,subQ55,subQ54,subQ53,subQ52])],"isStart":false});Q0=makeQuery(id+"F5.boolean.opBoolean","SPLIT",FACE,{"disambiguationData":[TD([subQ49])],"derivedFrom":makeQuery(id+"FRBVWJomYvBm3HE_1.boolean.opBoolean","SPLIT",FACE,{"disambiguationData":[TD([subQ49])],"derivedFrom":subQ90})});}
            var sketch = newSketch(context, id + "F14", { "sketchPlane" : qUnion([Q0])});
            skLineSegment(sketch, "E101", {"start": v(-23.01, 14.95) * mm, "end": v(-25.02, 14.95) * mm});
            skLineSegment(sketch, "E102", {"start": v(-25.02, 14.95) * mm, "end": v(-25.02, 13.97) * mm});
            skLineSegment(sketch, "E103", {"start": v(-25.02, 13.97) * mm, "end": v(-25.46, 13.97) * mm});
            skSolve(sketch);
        }
        {
            var Q0;
            {var subQ0=sQuery(id+"F14.wireOp",EDGE,"E103");Q0=makeQuery(id+"F14.imprint","IMPRINT",FACE,{"disambiguationData":[TD([[makeQuery(id+"F14.imprint","IMPRINT",EDGE,{"derivedFrom":subQ0}),-1.0]])]});}
            extrude(context, id + "F15", {"entities" : qUnion([Q0]), "operationType" : NewBodyOperationType.REMOVE, "oppositeDirection" : true, "depth" : 25 * mm});
        }
        {
            var Q0;
            {var subQ0=sQuery(id+"F14.wireOp",EDGE,"E101");Q0=makeQuery(id+"F14.imprint","IMPRINT",FACE,{"disambiguationData":[TD([[makeQuery(id+"F14.imprint","IMPRINT",EDGE,{"derivedFrom":subQ0}),1.0]])]});}
            extrude(context, id + "F16", {"entities" : qUnion([Q0]), "operationType" : NewBodyOperationType.ADD, "oppositeDirection" : true, "depth" : 5 * mm});
        }
        {
            var Q0;
            {var subQ0=sQuery(id+"F14.wireOp",EDGE,"E103");Q0=makeQuery(id+"F14.imprint","IMPRINT",FACE,{"disambiguationData":[TD([[makeQuery(id+"F14.imprint","IMPRINT",EDGE,{"derivedFrom":subQ0}),1.0]])]});}
            var sketch = newSketch(context, id + "F17", { "sketchPlane" : qUnion([Q0])});
            skLineSegment(sketch, "E104", {"start": v(-21.23, 16.62) * mm, "end": v(-21.23, 17.1) * mm});
            skLineSegment(sketch, "E105", {"start": v(-21.23, 17.1) * mm, "end": v(-20.68, 17.1) * mm});
            skLineSegment(sketch, "E106", {"start": v(-20.68, 17.1) * mm, "end": v(-20.68, 16.62) * mm});
            skLineSegment(sketch, "E107", {"start": v(-20.68, 16.62) * mm, "end": v(-21.23, 16.62) * mm});
            skLineSegment(sketch, "E108", {"start": v(-21.23, 15.62) * mm, "end": v(-20.68, 15.62) * mm});
            skLineSegment(sketch, "E109", {"start": v(-20.68, 15.62) * mm, "end": v(-20.68, 15.14) * mm});
            skLineSegment(sketch, "E110", {"start": v(-20.68, 15.14) * mm, "end": v(-21.23, 15.14) * mm});
            skLineSegment(sketch, "E111", {"start": v(-21.23, 15.14) * mm, "end": v(-21.23, 15.62) * mm});
            skLineSegment(sketch, "E112", {"start": v(20.21, 16.62) * mm, "end": v(20.21, 17.1) * mm});
            skLineSegment(sketch, "E113", {"start": v(20.21, 17.1) * mm, "end": v(20.77, 17.1) * mm});
            skLineSegment(sketch, "E114", {"start": v(20.77, 17.1) * mm, "end": v(20.77, 16.62) * mm});
            skLineSegment(sketch, "E115", {"start": v(20.77, 16.62) * mm, "end": v(20.21, 16.62) * mm});
            skLineSegment(sketch, "E116", {"start": v(20.23, 15.14) * mm, "end": v(20.23, 15.62) * mm});
            skLineSegment(sketch, "E117", {"start": v(20.23, 15.62) * mm, "end": v(20.78, 15.62) * mm});
            skLineSegment(sketch, "E118", {"start": v(20.78, 15.62) * mm, "end": v(20.78, 15.14) * mm});
            skLineSegment(sketch, "E119", {"start": v(20.78, 15.14) * mm, "end": v(20.23, 15.14) * mm});
            skSolve(sketch);
        }
        {
            var Q0;
            Q0=makeQuery(id+"F17.imprint","IMPRINT",FACE,{"disambiguationData":[TD([[makeQuery(id+"F17.imprint","IMPRINT",EDGE,{"derivedFrom":sQuery(id+"F17.wireOp",EDGE,"E104")}),-1.0]])]});
            var Q1;
            Q1=makeQuery(id+"F17.imprint","IMPRINT",FACE,{"disambiguationData":[TD([[makeQuery(id+"F17.imprint","IMPRINT",EDGE,{"derivedFrom":sQuery(id+"F17.wireOp",EDGE,"E108")}),-1.0]])]});
            var Q2;
            Q2=makeQuery(id+"F17.imprint","IMPRINT",FACE,{"disambiguationData":[TD([[makeQuery(id+"F17.imprint","IMPRINT",EDGE,{"derivedFrom":sQuery(id+"F17.wireOp",EDGE,"E112")}),-1.0]])]});
            var Q3;
            Q3=makeQuery(id+"F17.imprint","IMPRINT",FACE,{"disambiguationData":[TD([[makeQuery(id+"F17.imprint","IMPRINT",EDGE,{"derivedFrom":sQuery(id+"F17.wireOp",EDGE,"E116")}),-1.0]])]});
            extrude(context, id + "F18", {"entities" : qUnion([Q0, Q1, Q2, Q3]), "operationType" : NewBodyOperationType.REMOVE, "oppositeDirection" : true, "depth" : .1 * mm});
        }
    });
